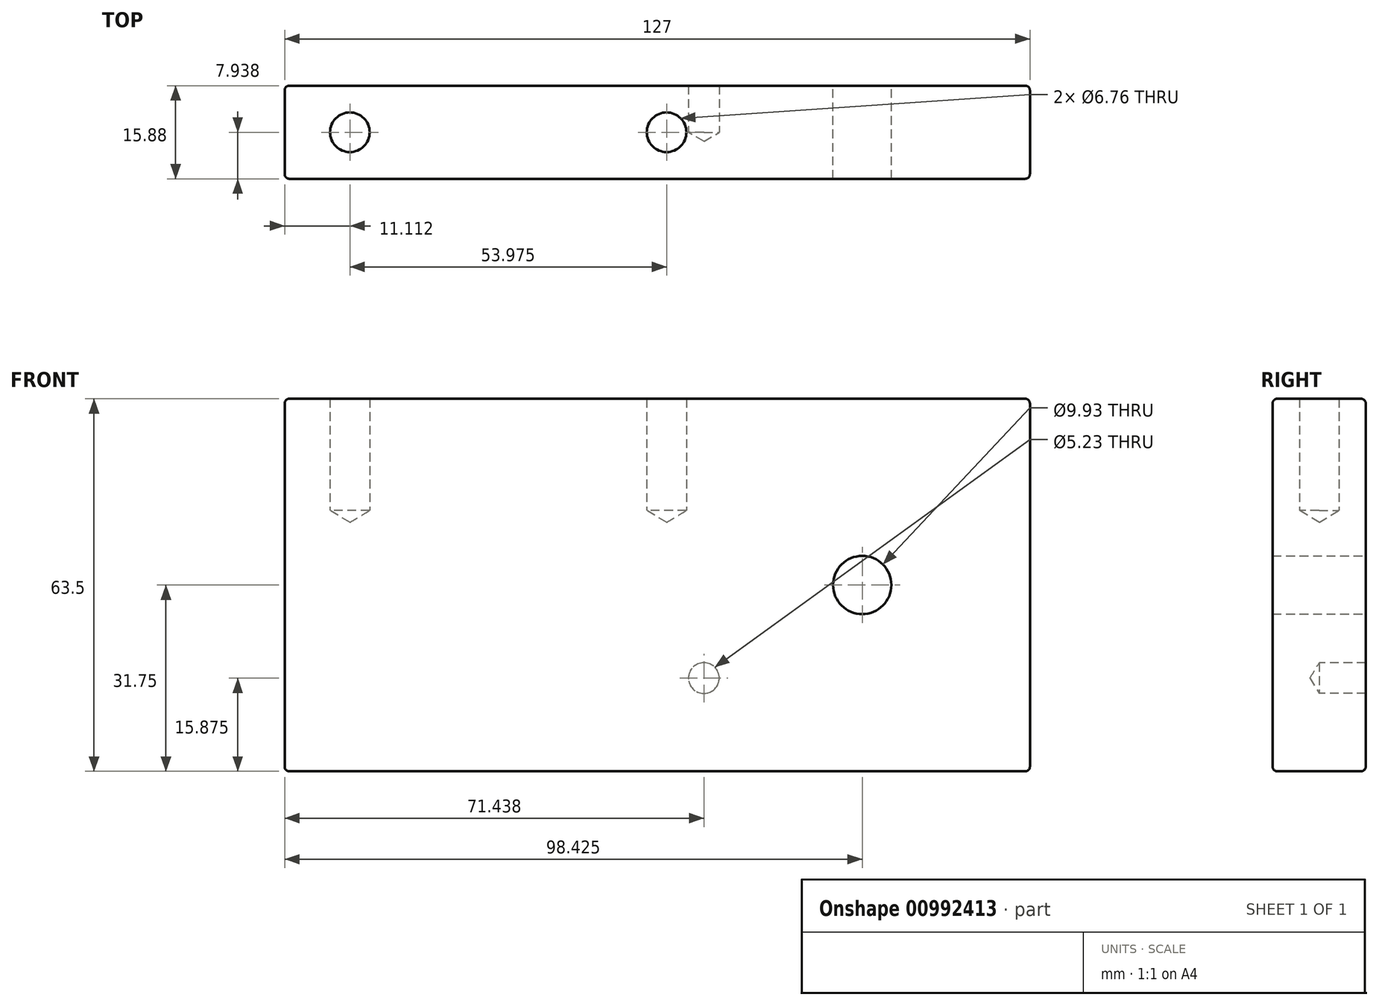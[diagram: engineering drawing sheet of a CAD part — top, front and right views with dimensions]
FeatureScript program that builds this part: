
annotation { "Feature Type Name" : "Feature", "Feature Type Description" : "" }
export const myFeature = defineFeature(function(context is Context, id is Id, definition is map)
    precondition{}
    {
        {
            var Q0;
            Q0=qCreatedBy(makeId("Front.planeOp"),FACE);
            var sketch = newSketch(context, id + "F0", { "sketchPlane" : qUnion([Q0])});
            skLineSegment(sketch, "E0.bottom", {"start": v(63.5, 31.75) * mm, "end": v(-63.5, 31.75) * mm});
            skLineSegment(sketch, "E0.top", {"start": v(63.5, -31.75) * mm, "end": v(-63.5, -31.75) * mm});
            skLineSegment(sketch, "E0.left", {"start": v(63.5, 31.75) * mm, "end": v(63.5, -31.75) * mm});
            skLineSegment(sketch, "E0.right", {"start": v(-63.5, 31.75) * mm, "end": v(-63.5, -31.75) * mm});
            skPoint(sketch, "E0.middle", {"position": v(0, 0) * mm});
            skSolve(sketch);
        }
        {
            var Q0;
            Q0=makeQuery(id+"F0.imprint","IMPRINT",FACE,{"disambiguationData":[TD([[makeQuery(id+"F0.imprint","IMPRINT",EDGE,{"derivedFrom":sQuery(id+"F0.wireOp",EDGE,"E0.bottom")}),1.0]])]});
            extrude(context, id + "F1", {"entities" : qUnion([Q0]), "oppositeDirection" : true, "depth" : 15.88 * mm, "offsetDistance" : 25.4 * mm});
        }
        {
            var Q0;
            Q0=makeQuery(id+"F1.opExtrude","SWEPT_FACE",FACE,{"disambiguationData":[OSD([sQuery(id+"F0.wireOp",EDGE,"E0.bottom")])]});
            var sketch = newSketch(context, id + "F2", { "sketchPlane" : qUnion([Q0])});
            skCircle(sketch, "E1", {"center": v(-52.39, 7.94) * mm, "radius": 3.57 * mm});
            skPoint(sketch, "E1.centerSnap0", {"position": v(-63.5, 7.94) * mm});
            skCircle(sketch, "E2", {"center": v(1.59, 7.94) * mm, "radius": 3.57 * mm});
            skSolve(sketch);
        }
        {
            var Q0;
            Q0=sQuery(id+"F2.wireOp",VERTEX,"E1.center");
            var Q1;
            Q1=sQuery(id+"F2.wireOp",VERTEX,"E2.center");
            var Q2;
            Q2=makeQuery(id+"F1.opExtrude","SWEPT_BODY",BODY,{"disambiguationData":[OSD([sQuery(id+"F0.wireOp",EDGE,"E0.bottom"),sQuery(id+"F0.wireOp",EDGE,"E0.top"),sQuery(id+"F0.wireOp",EDGE,"E0.left"),sQuery(id+"F0.wireOp",EDGE,"E0.right")])]});
            hole(context, id + "F3", {"style" : HoleStyle.SIMPLE, "endStyle" : HoleEndStyle.BLIND, "standardTappedOrClearance" : lookupTablePath({ "fit" : "Close (ASME)", "standard" : "ANSI", "size" : "1/4", "type" : "Clearance" }), "standardBlindInLast" : lookupTablePath({ "fit" : "Close", "standard" : "ANSI", "engagement" : "75%", "pitch" : "20 tpi", "size" : "1/4", "type" : "Clearance & tapped" }), "holeDiameter" : 6.76 * mm, "majorDiameter" : 6.35 * mm, "holeDepth" : 19.05 * mm, "isTappedThrough" : true, "tappedDepth" : 12.7 * mm, "tapClearance" : 3, "locations" : qUnion([Q0, Q1]), "scope" : qUnion([Q2]), "startStyle" : HoleStartStyle.SKETCH});
        }
        {
            var Q0;
            Q0=makeQuery(id+"F0.imprint","IMPRINT",FACE,{"disambiguationData":[TD([[makeQuery(id+"F0.imprint","IMPRINT",EDGE,{"derivedFrom":sQuery(id+"F0.wireOp",EDGE,"E0.bottom")}),1.0]])]});
            var sketch = newSketch(context, id + "F4", { "sketchPlane" : qUnion([Q0])});
            skCircle(sketch, "E3", {"center": v(34.92, 0) * mm, "radius": 5.16 * mm});
            skSolve(sketch);
        }
        {
            var Q0;
            Q0=sQuery(id+"F4.wireOp",VERTEX,"E3.center");
            var Q1;
            Q1=makeQuery(id+"F1.opExtrude","SWEPT_BODY",BODY,{"disambiguationData":[OSD([sQuery(id+"F0.wireOp",EDGE,"E0.bottom"),sQuery(id+"F0.wireOp",EDGE,"E0.top"),sQuery(id+"F0.wireOp",EDGE,"E0.left"),sQuery(id+"F0.wireOp",EDGE,"E0.right")])]});
            hole(context, id + "F5", {"style" : HoleStyle.SIMPLE, "endStyle" : HoleEndStyle.THROUGH, "standardTappedOrClearance" : lookupTablePath({ "fit" : "Close (ASME)", "standard" : "ANSI", "size" : "3/8", "type" : "Clearance" }), "standardBlindInLast" : lookupTablePath({ "fit" : "Close", "standard" : "ANSI", "engagement" : "75%", "pitch" : "16 tpi", "size" : "3/8", "type" : "Clearance & tapped" }), "holeDiameter" : 9.93 * mm, "majorDiameter" : 6.35 * mm, "isTappedThrough" : true, "tappedDepth" : 12.7 * mm, "tapClearance" : 3, "locations" : qUnion([Q0]), "scope" : qUnion([Q1]), "startStyle" : HoleStartStyle.SKETCH});
        }
        {
            var Q0;
            Q0=makeQuery(id+"F1.opExtrude","CAP_FACE",FACE,{"disambiguationData":[OSD([sQuery(id+"F0.wireOp",EDGE,"E0.bottom"),sQuery(id+"F0.wireOp",EDGE,"E0.top"),sQuery(id+"F0.wireOp",EDGE,"E0.left"),sQuery(id+"F0.wireOp",EDGE,"E0.right")])],"isStart":false});
            var sketch = newSketch(context, id + "F6", { "sketchPlane" : qUnion([Q0])});
            skCircle(sketch, "E4", {"center": v(-7.94, -15.88) * mm, "radius": 1.59 * mm});
            skSolve(sketch);
        }
        {
            var Q0;
            Q0=sQuery(id+"F6.wireOp",VERTEX,"E4.center");
            var Q1;
            Q1=makeQuery(id+"F1.opExtrude","SWEPT_BODY",BODY,{"disambiguationData":[OSD([sQuery(id+"F0.wireOp",EDGE,"E0.bottom"),sQuery(id+"F0.wireOp",EDGE,"E0.top"),sQuery(id+"F0.wireOp",EDGE,"E0.left"),sQuery(id+"F0.wireOp",EDGE,"E0.right")])]});
            hole(context, id + "F7", {"style" : HoleStyle.SIMPLE, "endStyle" : HoleEndStyle.BLIND, "standardTappedOrClearance" : lookupTablePath({ "fit" : "Close (ASME)", "standard" : "ANSI", "size" : "#10", "type" : "Clearance" }), "standardBlindInLast" : lookupTablePath({ "fit" : "Close", "standard" : "ANSI", "engagement" : "75%", "pitch" : "24 tpi", "size" : "#10", "type" : "Clearance & tapped" }), "holeDiameter" : 5.23 * mm, "majorDiameter" : 6.35 * mm, "holeDepth" : 7.94 * mm, "isTappedThrough" : true, "tappedDepth" : 12.7 * mm, "tapClearance" : 3, "locations" : qUnion([Q0]), "scope" : qUnion([Q1]), "startStyle" : HoleStartStyle.SKETCH});
        }
        {
            var Q0;
            Q0=makeQuery(id+"F1.opExtrude","CAP_EDGE",EDGE,{"disambiguationData":[OSD([sQuery(id+"F0.wireOp",EDGE,"E0.bottom")])],"isStart":true});
            var Q1;
            Q1=makeQuery(id+"F1.opExtrude","SWEPT_EDGE",EDGE,{"disambiguationData":[OSD([sQuery(id+"F0.wireOp",EDGE,"E0.bottom"),sQuery(id+"F0.wireOp",EDGE,"E0.right")])]});
            var Q2;
            Q2=makeQuery(id+"F1.opExtrude","CAP_EDGE",EDGE,{"disambiguationData":[OSD([sQuery(id+"F0.wireOp",EDGE,"E0.bottom")])],"isStart":false});
            var Q3;
            Q3=makeQuery(id+"F1.opExtrude","SWEPT_EDGE",EDGE,{"disambiguationData":[OSD([sQuery(id+"F0.wireOp",EDGE,"E0.bottom"),sQuery(id+"F0.wireOp",EDGE,"E0.left")])]});
            var Q4;
            Q4=makeQuery(id+"F1.opExtrude","CAP_EDGE",EDGE,{"disambiguationData":[OSD([sQuery(id+"F0.wireOp",EDGE,"E0.left")])],"isStart":true});
            var Q5;
            Q5=makeQuery(id+"F1.opExtrude","CAP_EDGE",EDGE,{"disambiguationData":[OSD([sQuery(id+"F0.wireOp",EDGE,"E0.left")])],"isStart":false});
            var Q6;
            Q6=makeQuery(id+"F1.opExtrude","CAP_EDGE",EDGE,{"disambiguationData":[OSD([sQuery(id+"F0.wireOp",EDGE,"E0.right")])],"isStart":false});
            var Q7;
            Q7=makeQuery(id+"F1.opExtrude","CAP_EDGE",EDGE,{"disambiguationData":[OSD([sQuery(id+"F0.wireOp",EDGE,"E0.right")])],"isStart":true});
            var Q8;
            Q8=makeQuery(id+"F1.opExtrude","SWEPT_EDGE",EDGE,{"disambiguationData":[OSD([sQuery(id+"F0.wireOp",EDGE,"E0.top"),sQuery(id+"F0.wireOp",EDGE,"E0.right")])]});
            var Q9;
            Q9=makeQuery(id+"F1.opExtrude","CAP_EDGE",EDGE,{"disambiguationData":[OSD([sQuery(id+"F0.wireOp",EDGE,"E0.top")])],"isStart":false});
            var Q10;
            Q10=makeQuery(id+"F1.opExtrude","CAP_EDGE",EDGE,{"disambiguationData":[OSD([sQuery(id+"F0.wireOp",EDGE,"E0.top")])],"isStart":true});
            var Q11;
            Q11=makeQuery(id+"F1.opExtrude","SWEPT_EDGE",EDGE,{"disambiguationData":[OSD([sQuery(id+"F0.wireOp",EDGE,"E0.top"),sQuery(id+"F0.wireOp",EDGE,"E0.left")])]});
            fillet(context, id + "F8", {"entities" : qUnion([Q0, Q1, Q2, Q3, Q4, Q5, Q6, Q7, Q8, Q9, Q10, Q11]), "radius" : 0.8 * mm, "tangentPropagation" : true, "allowEdgeOverflow" : false});
        }
    });
